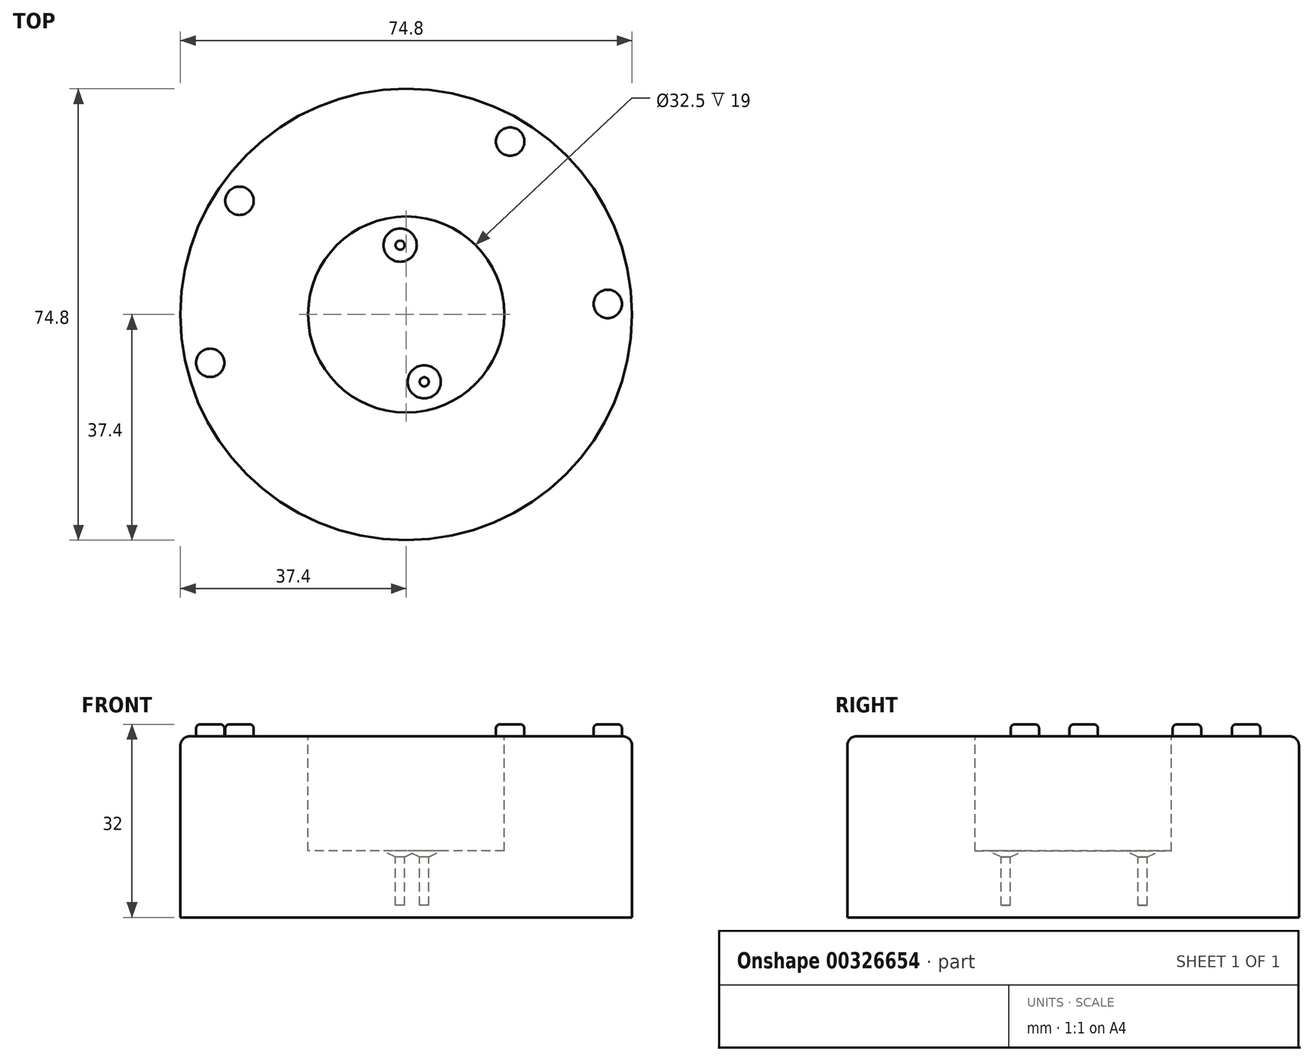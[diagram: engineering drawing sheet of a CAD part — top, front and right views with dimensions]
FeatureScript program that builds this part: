
annotation { "Feature Type Name" : "Feature", "Feature Type Description" : "" }
export const myFeature = defineFeature(function(context is Context, id is Id, definition is map)
    precondition{}
    {
        {
            var Q0;
            Q0=qCreatedBy(makeId("Top.planeOp"),FACE);
            var sketch = newSketch(context, id + "F0", { "sketchPlane" : qUnion([Q0])});
            skCircle(sketch, "E0", {"center": v(0, 0) * mm, "radius": 37.4 * mm});
            skSolve(sketch);
        }
        {
            var Q0;
            Q0=makeQuery(id+"F0.imprint","IMPRINT",FACE,{"disambiguationData":[TD([[makeQuery(id+"F0.imprint","IMPRINT",EDGE,{"derivedFrom":sQuery(id+"F0.wireOp",EDGE,"E0")}),1.0]])]});
            extrude(context, id + "F1", {"entities" : qUnion([Q0]), "depth" : 30 * mm});
        }
        {
            var Q0;
            Q0=makeQuery(id+"F1.opExtrude","CAP_FACE",FACE,{"disambiguationData":[OSD([sQuery(id+"F0.wireOp",EDGE,"E0")])],"isStart":false});
            var sketch = newSketch(context, id + "F2", { "sketchPlane" : qUnion([Q0]), "disableImprinting" : false});
            skCircle(sketch, "E1", {"center": v(0, 0) * mm, "radius": 16.25 * mm});
            skCircle(sketch, "E2", {"center": v(-27.62, 18.85) * mm, "radius": 2.35 * mm});
            skCircle(sketch, "E3", {"center": v(-32.46, -8) * mm, "radius": 2.35 * mm});
            skCircle(sketch, "E4", {"center": v(17.22, 28.66) * mm, "radius": 2.35 * mm});
            skCircle(sketch, "E5", {"center": v(33.39, 1.76) * mm, "radius": 2.35 * mm});
            skCircle(sketch, "E6", {"center": v(-1.01, 11.5) * mm, "radius": 0.75 * mm});
            skCircle(sketch, "E7", {"center": v(2.98, -11.15) * mm, "radius": 0.75 * mm});
            skSolve(sketch);
        }
        {
            var Q0;
            Q0=makeQuery(id+"F2.imprint","IMPRINT",FACE,{"disambiguationData":[TD([[makeQuery(id+"F2.imprint","IMPRINT",EDGE,{"derivedFrom":sQuery(id+"F2.wireOp",EDGE,"E2")}),1.0]])]});
            var Q1;
            Q1=makeQuery(id+"F2.imprint","IMPRINT",FACE,{"disambiguationData":[TD([[makeQuery(id+"F2.imprint","IMPRINT",EDGE,{"derivedFrom":sQuery(id+"F2.wireOp",EDGE,"E5")}),1.0]])]});
            var Q2;
            Q2=makeQuery(id+"F2.imprint","IMPRINT",FACE,{"disambiguationData":[TD([[makeQuery(id+"F2.imprint","IMPRINT",EDGE,{"derivedFrom":sQuery(id+"F2.wireOp",EDGE,"E4")}),1.0]])]});
            var Q3;
            Q3=makeQuery(id+"F2.imprint","IMPRINT",FACE,{"disambiguationData":[TD([[makeQuery(id+"F2.imprint","IMPRINT",EDGE,{"derivedFrom":sQuery(id+"F2.wireOp",EDGE,"E3")}),1.0]])]});
            extrude(context, id + "F3", {"entities" : qUnion([Q0, Q1, Q2, Q3]), "operationType" : NewBodyOperationType.ADD, "depth" : 2 * mm});
        }
        {
            var Q0;
            Q0=makeQuery(id+"F2.imprint","IMPRINT",FACE,{"disambiguationData":[TD([[makeQuery(id+"F2.imprint","IMPRINT",EDGE,{"derivedFrom":sQuery(id+"F2.wireOp",EDGE,"E6")}),1.0]])]});
            var Q1;
            Q1=makeQuery(id+"F2.imprint","IMPRINT",FACE,{"disambiguationData":[TD([[makeQuery(id+"F2.imprint","IMPRINT",EDGE,{"derivedFrom":sQuery(id+"F2.wireOp",EDGE,"E1")}),1.0]])]});
            var Q2;
            Q2=makeQuery(id+"F2.imprint","IMPRINT",FACE,{"disambiguationData":[TD([[makeQuery(id+"F2.imprint","IMPRINT",EDGE,{"derivedFrom":sQuery(id+"F2.wireOp",EDGE,"E7")}),1.0]])]});
            extrude(context, id + "F4", {"entities" : qUnion([Q0, Q1, Q2]), "operationType" : NewBodyOperationType.REMOVE, "oppositeDirection" : true, "depth" : 19 * mm});
        }
        {
            var Q0;
            Q0=makeQuery(id+"F2.imprint","IMPRINT",FACE,{"disambiguationData":[TD([[makeQuery(id+"F2.imprint","IMPRINT",EDGE,{"derivedFrom":sQuery(id+"F2.wireOp",EDGE,"E6")}),1.0]])]});
            var Q1;
            Q1=makeQuery(id+"F2.imprint","IMPRINT",FACE,{"disambiguationData":[TD([[makeQuery(id+"F2.imprint","IMPRINT",EDGE,{"derivedFrom":sQuery(id+"F2.wireOp",EDGE,"E7")}),1.0]])]});
            extrude(context, id + "F5", {"entities" : qUnion([Q0, Q1]), "operationType" : NewBodyOperationType.REMOVE, "oppositeDirection" : true, "depth" : 28 * mm});
        }
        {
            var Q0;
            Q0=makeQuery(id+"F5.boolean.opBoolean","INTERSECT",EDGE,{"derivedFrom":[makeQuery(id+"F4.boolean.opBoolean","COPY",FACE,{"derivedFrom":makeQuery(id+"F4.opExtrude","CAP_FACE",FACE,{"disambiguationData":[OSD([sQuery(id+"F2.wireOp",EDGE,"E1")])],"isStart":false})}),makeQuery(id+"F5.opExtrude","SWEPT_FACE",FACE,{"disambiguationData":[OSD([sQuery(id+"F2.wireOp",EDGE,"E6")])]})]});
            var Q1;
            Q1=makeQuery(id+"F5.boolean.opBoolean","INTERSECT",EDGE,{"derivedFrom":[makeQuery(id+"F4.boolean.opBoolean","COPY",FACE,{"derivedFrom":makeQuery(id+"F4.opExtrude","CAP_FACE",FACE,{"disambiguationData":[OSD([sQuery(id+"F2.wireOp",EDGE,"E1")])],"isStart":false})}),makeQuery(id+"F5.opExtrude","SWEPT_FACE",FACE,{"disambiguationData":[OSD([sQuery(id+"F2.wireOp",EDGE,"E7")])]})]});
            chamfer(context, id + "F6", {"entities" : qUnion([Q0, Q1]), "chamferType" : ChamferType.TWO_OFFSETS, "width1" : 2 * mm, "oppositeDirection" : false, "width2" : 1 * mm, "tangentPropagation" : true});
        }
        {
            var Q0;
            Q0=makeQuery(id+"F1.opExtrude","CAP_EDGE",EDGE,{"disambiguationData":[OSD([sQuery(id+"F0.wireOp",EDGE,"E0")])],"isStart":false});
            var Q1;
            Q1=makeQuery(id+"F4.boolean.opBoolean","COPY",EDGE,{"derivedFrom":makeQuery(id+"F4.opExtrude","CAP_EDGE",EDGE,{"disambiguationData":[OSD([sQuery(id+"F2.wireOp",EDGE,"E1")])],"isStart":true})});
            fillet(context, id + "F7", {"entities" : qUnion([Q0, Q1]), "radius" : 1.5 * mm, "tangentPropagation" : true, "allowEdgeOverflow" : false});
        }
        {
            var Q0;
            Q0=makeQuery(id+"F3.opExtrude","CAP_FACE",FACE,{"disambiguationData":[OSD([sQuery(id+"F2.wireOp",EDGE,"E2")])],"isStart":false});
            var Q1;
            Q1=makeQuery(id+"F3.opExtrude","CAP_FACE",FACE,{"disambiguationData":[OSD([sQuery(id+"F2.wireOp",EDGE,"E4")])],"isStart":false});
            var Q2;
            Q2=makeQuery(id+"F3.opExtrude","CAP_FACE",FACE,{"disambiguationData":[OSD([sQuery(id+"F2.wireOp",EDGE,"E5")])],"isStart":false});
            var Q3;
            Q3=makeQuery(id+"F3.opExtrude","CAP_FACE",FACE,{"disambiguationData":[OSD([sQuery(id+"F2.wireOp",EDGE,"E3")])],"isStart":false});
            fillet(context, id + "F8", {"entities" : qUnion([Q0, Q1, Q2, Q3]), "radius" : .7 * mm, "tangentPropagation" : true, "allowEdgeOverflow" : false});
        }
    });
